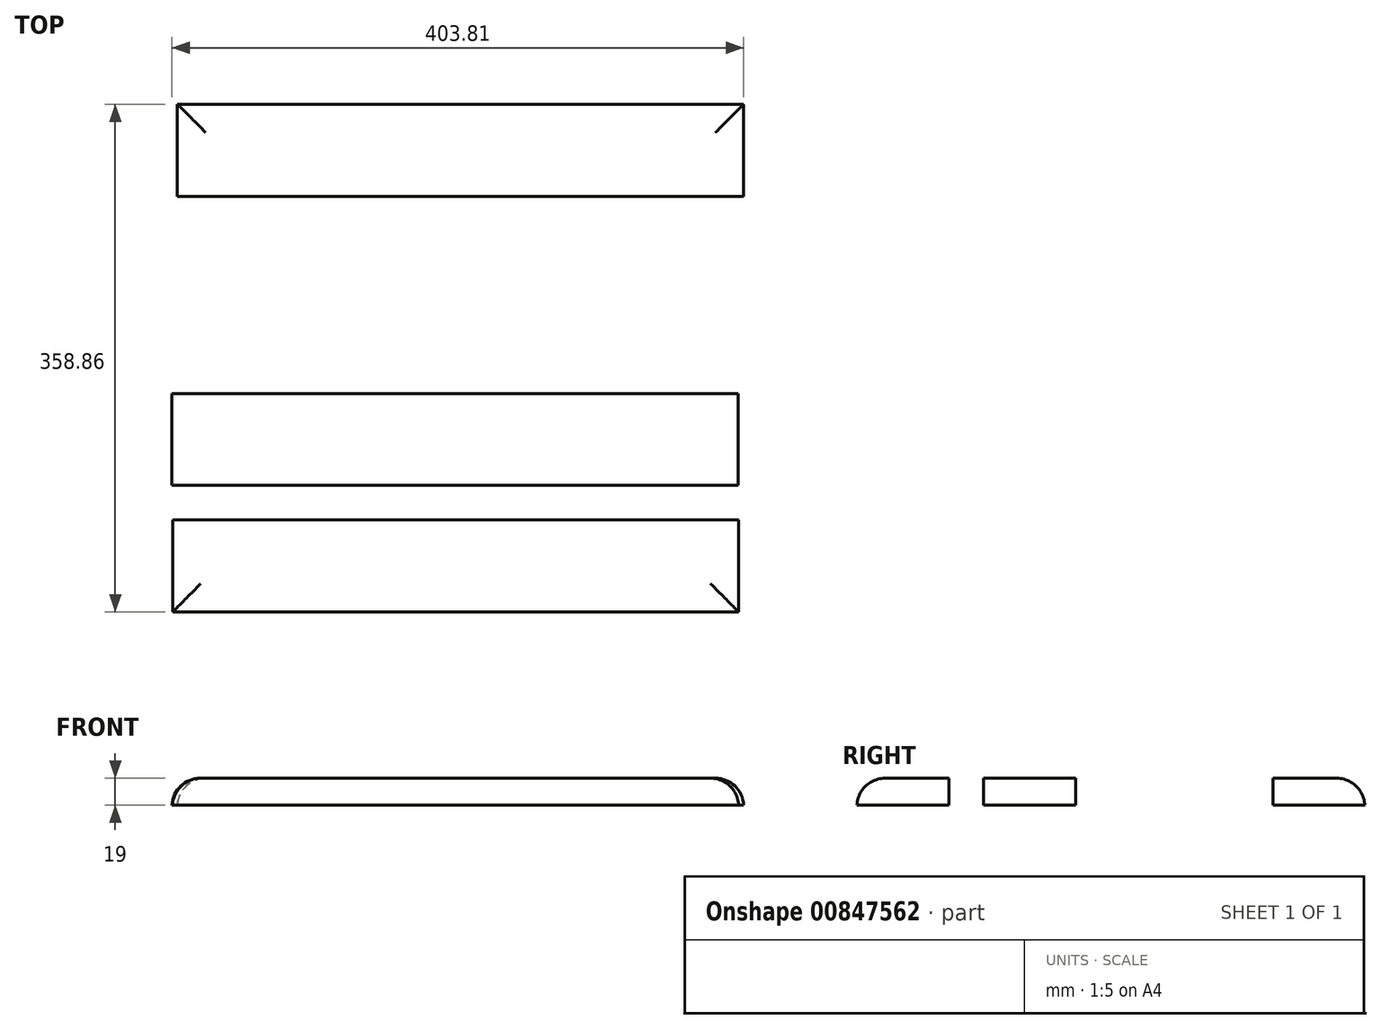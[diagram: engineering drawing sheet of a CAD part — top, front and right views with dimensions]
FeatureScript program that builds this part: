
annotation { "Feature Type Name" : "Feature", "Feature Type Description" : "" }
export const myFeature = defineFeature(function(context is Context, id is Id, definition is map)
    precondition{}
    {
        {
            var Q0;
            Q0=qCreatedBy(makeId("Top.planeOp"),FACE);
            var sketch = newSketch(context, id + "F0", { "sketchPlane" : qUnion([Q0])});
            skLineSegment(sketch, "E0.bottom", {"start": v(-284.91, 201.01) * mm, "end": v(115.09, 201.01) * mm});
            skLineSegment(sketch, "E0.top", {"start": v(-284.91, 136.01) * mm, "end": v(115.09, 136.01) * mm});
            skLineSegment(sketch, "E0.left", {"start": v(-284.91, 201.01) * mm, "end": v(-284.91, 136.01) * mm});
            skLineSegment(sketch, "E0.right", {"start": v(115.09, 201.01) * mm, "end": v(115.09, 136.01) * mm});
            skLineSegment(sketch, "E1.bottom", {"start": v(-284.91, 36.22) * mm, "end": v(115.09, 36.22) * mm});
            skLineSegment(sketch, "E1.top", {"start": v(-284.91, -28.78) * mm, "end": v(115.09, -28.78) * mm});
            skLineSegment(sketch, "E1.left", {"start": v(-284.91, 36.22) * mm, "end": v(-284.91, -28.78) * mm});
            skLineSegment(sketch, "E1.right", {"start": v(115.09, 36.22) * mm, "end": v(115.09, -28.78) * mm});
            skLineSegment(sketch, "E2.bottom", {"start": v(-252.58, -136.4) * mm, "end": v(147.42, -136.4) * mm});
            skLineSegment(sketch, "E2.top", {"start": v(-252.58, -201.4) * mm, "end": v(147.42, -201.4) * mm});
            skLineSegment(sketch, "E2.left", {"start": v(-252.58, -136.4) * mm, "end": v(-252.58, -201.4) * mm});
            skLineSegment(sketch, "E2.right", {"start": v(147.42, -136.4) * mm, "end": v(147.42, -201.4) * mm});
            skSolve(sketch);
        }
        {
            var Q0;
            Q0=makeQuery(id+"F0.imprint","IMPRINT",FACE,{"disambiguationData":[TD([[makeQuery(id+"F0.imprint","IMPRINT",EDGE,{"derivedFrom":sQuery(id+"F0.wireOp",EDGE,"E0.bottom")}),-1.0]])]});
            extrude(context, id + "F1", {"entities" : qUnion([Q0]), "depth" : 19 * mm, "offsetDistance" : 25 * mm});
        }
        {
            var Q0;
            Q0=qCreatedBy(makeId("Top.planeOp"),FACE);
            var sketch = newSketch(context, id + "F2", { "sketchPlane" : qUnion([Q0])});
            skLineSegment(sketch, "E3.bottom", {"start": v(111.28, -68.39) * mm, "end": v(-288.72, -68.39) * mm});
            skLineSegment(sketch, "E3.top", {"start": v(111.28, -3.39) * mm, "end": v(-288.72, -3.39) * mm});
            skLineSegment(sketch, "E3.left", {"start": v(111.28, -68.39) * mm, "end": v(111.28, -3.39) * mm});
            skLineSegment(sketch, "E3.right", {"start": v(-288.72, -68.39) * mm, "end": v(-288.72, -3.39) * mm});
            skSolve(sketch);
        }
        {
            var Q0;
            Q0=makeQuery(id+"F2.imprint","IMPRINT",FACE,{"disambiguationData":[TD([[makeQuery(id+"F2.imprint","IMPRINT",EDGE,{"derivedFrom":sQuery(id+"F2.wireOp",EDGE,"E3.bottom")}),-1.0]])]});
            extrude(context, id + "F3", {"entities" : qUnion([Q0]), "depth" : 19 * mm, "offsetDistance" : 25 * mm});
        }
        {
            var Q0;
            Q0=qCreatedBy(makeId("Top.planeOp"),FACE);
            var sketch = newSketch(context, id + "F4", { "sketchPlane" : qUnion([Q0])});
            skLineSegment(sketch, "E4.bottom", {"start": v(111.62, -157.85) * mm, "end": v(-288.38, -157.85) * mm});
            skLineSegment(sketch, "E4.top", {"start": v(111.62, -92.85) * mm, "end": v(-288.38, -92.85) * mm});
            skLineSegment(sketch, "E4.left", {"start": v(111.62, -157.85) * mm, "end": v(111.62, -92.85) * mm});
            skLineSegment(sketch, "E4.right", {"start": v(-288.38, -157.85) * mm, "end": v(-288.38, -92.85) * mm});
            skSolve(sketch);
        }
        {
            var Q0;
            Q0 = qSketchRegion(id + "F4", true);
            extrude(context, id + "F5", {"entities" : qUnion([Q0]), "depth" : 19 * mm, "offsetDistance" : 25 * mm});
        }
        {
            var Q0;
            Q0=makeQuery(id+"F1.opExtrude","CAP_EDGE",EDGE,{"disambiguationData":[OSD([sQuery(id+"F0.wireOp",EDGE,"E0.right")])],"isStart":false});
            fillet(context, id + "F6", {"entities" : qUnion([Q0]), "radius" : 20 * mm, "tangentPropagation" : true, "allowEdgeOverflow" : false});
        }
        {
            var Q0;
            Q0=makeQuery(id+"F3.opExtrude","CAP_EDGE",EDGE,{"disambiguationData":[OSD([sQuery(id+"F2.wireOp",EDGE,"E3.left")])],"isStart":false});
            fillet(context, id + "F7", {"entities" : qUnion([Q0]), "radius" : 20 * mm, "tangentPropagation" : true, "allowEdgeOverflow" : false});
        }
        {
            var Q0;
            Q0=makeQuery(id+"F5.opExtrude","CAP_EDGE",EDGE,{"disambiguationData":[OSD([sQuery(id+"F4.wireOp",EDGE,"E4.left")])],"isStart":false});
            fillet(context, id + "F8", {"entities" : qUnion([Q0]), "radius" : 20 * mm, "tangentPropagation" : true, "allowEdgeOverflow" : false});
        }
        {
            var Q0;
            Q0=makeQuery(id+"F5.opExtrude","CAP_EDGE",EDGE,{"disambiguationData":[OSD([sQuery(id+"F4.wireOp",EDGE,"E4.bottom")])],"isStart":false});
            fillet(context, id + "F9", {"entities" : qUnion([Q0]), "radius" : 20 * mm, "tangentPropagation" : true, "allowEdgeOverflow" : false});
        }
        {
            var Q0;
            Q0=makeQuery(id+"F5.opExtrude","CAP_EDGE",EDGE,{"disambiguationData":[OSD([sQuery(id+"F4.wireOp",EDGE,"E4.right")])],"isStart":false});
            fillet(context, id + "F10", {"entities" : qUnion([Q0]), "radius" : 20 * mm, "tangentPropagation" : true, "allowEdgeOverflow" : false});
        }
        {
            var Q0;
            Q0=makeQuery(id+"F3.opExtrude","CAP_EDGE",EDGE,{"disambiguationData":[OSD([sQuery(id+"F2.wireOp",EDGE,"E3.right")])],"isStart":false});
            fillet(context, id + "F11", {"entities" : qUnion([Q0]), "radius" : 20 * mm, "tangentPropagation" : true, "allowEdgeOverflow" : false});
        }
        {
            var Q0;
            Q0=makeQuery(id+"F1.opExtrude","CAP_EDGE",EDGE,{"disambiguationData":[OSD([sQuery(id+"F0.wireOp",EDGE,"E0.bottom")])],"isStart":false});
            fillet(context, id + "F12", {"entities" : qUnion([Q0]), "radius" : 20 * mm, "tangentPropagation" : true, "allowEdgeOverflow" : false});
        }
        {
            var Q0;
            Q0=makeQuery(id+"F1.opExtrude","CAP_EDGE",EDGE,{"disambiguationData":[OSD([sQuery(id+"F0.wireOp",EDGE,"E0.left")])],"isStart":false});
            fillet(context, id + "F13", {"entities" : qUnion([Q0]), "radius" : 20 * mm, "tangentPropagation" : true, "allowEdgeOverflow" : false});
        }
    });
